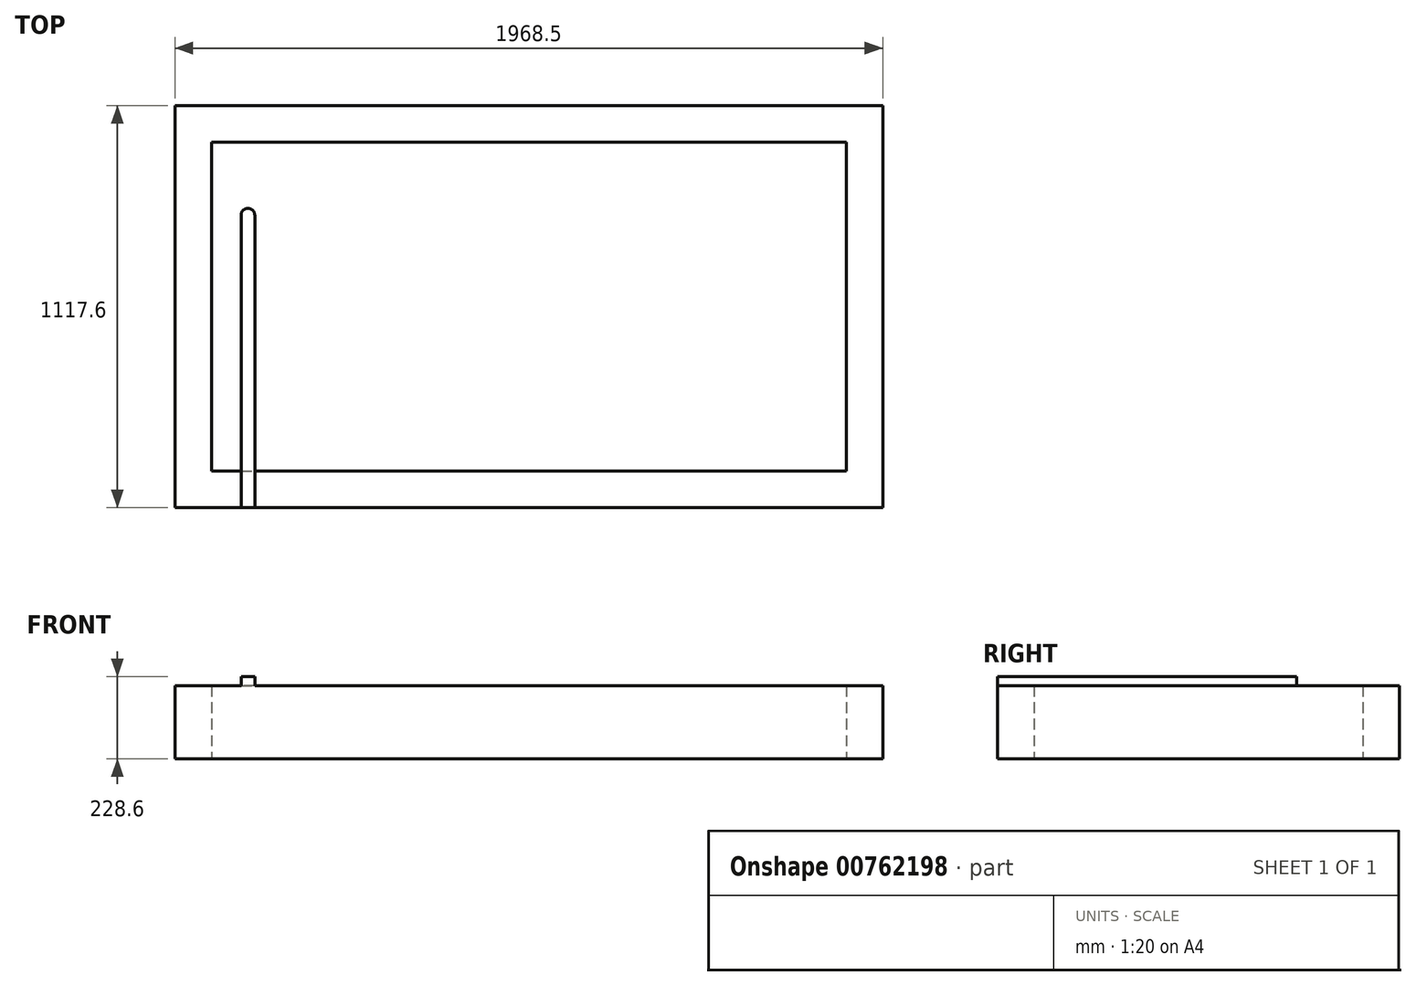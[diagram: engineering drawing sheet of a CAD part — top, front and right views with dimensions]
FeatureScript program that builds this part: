
annotation { "Feature Type Name" : "Feature", "Feature Type Description" : "" }
export const myFeature = defineFeature(function(context is Context, id is Id, definition is map)
    precondition{}
    {
        {
            var Q0;
            Q0=qCreatedBy(makeId("Top.planeOp"),FACE);
            var sketch = newSketch(context, id + "F0", { "sketchPlane" : qUnion([Q0])});
            skLineSegment(sketch, "E0.bottom", {"start": v(0, 0) * mm, "end": v(1968.5, 0) * mm});
            skLineSegment(sketch, "E0.top", {"start": v(0, -1117.6) * mm, "end": v(1968.5, -1117.6) * mm});
            skLineSegment(sketch, "E0.left", {"start": v(0, 0) * mm, "end": v(0, -1117.6) * mm});
            skLineSegment(sketch, "E0.right", {"start": v(1968.5, 0) * mm, "end": v(1968.5, -1117.6) * mm});
            skLineSegment(sketch, "E1.bottom", {"start": v(101.6, -101.6) * mm, "end": v(1866.9, -101.6) * mm});
            skLineSegment(sketch, "E1.top", {"start": v(101.6, -1016) * mm, "end": v(1866.9, -1016) * mm});
            skLineSegment(sketch, "E1.left", {"start": v(101.6, -101.6) * mm, "end": v(101.6, -1016) * mm});
            skLineSegment(sketch, "E1.right", {"start": v(1866.9, -101.6) * mm, "end": v(1866.9, -1016) * mm});
            skSolve(sketch);
        }
        {
            var Q0;
            Q0=makeQuery(id+"F0.imprint","IMPRINT",FACE,{"disambiguationData":[TD([[makeQuery(id+"F0.imprint","IMPRINT",EDGE,{"derivedFrom":sQuery(id+"F0.wireOp",EDGE,"E0.bottom")}),-1.0]])]});
            extrude(context, id + "F1", {"entities" : qUnion([Q0]), "depth" : 203.2 * mm, "offsetDistance" : 25.4 * mm});
        }
        {
            var Q0;
            Q0=makeQuery(id+"F1.opExtrude","CAP_FACE",FACE,{"disambiguationData":[OSD([sQuery(id+"F0.wireOp",EDGE,"E0.bottom"),sQuery(id+"F0.wireOp",EDGE,"E0.top"),sQuery(id+"F0.wireOp",EDGE,"E0.left"),sQuery(id+"F0.wireOp",EDGE,"E0.right"),sQuery(id+"F0.wireOp",EDGE,"E1.bottom"),sQuery(id+"F0.wireOp",EDGE,"E1.top"),sQuery(id+"F0.wireOp",EDGE,"E1.left"),sQuery(id+"F0.wireOp",EDGE,"E1.right")])],"isStart":false});
            var sketch = newSketch(context, id + "F2", { "sketchPlane" : qUnion([Q0])});
            skLineSegment(sketch, "E2", {"start": v(184.15, -304.8) * mm, "end": v(184.15, -1117.6) * mm});
            skLineSegment(sketch, "E3", {"start": v(222.25, -304.8) * mm, "end": v(222.25, -1117.6) * mm});
            skArc(sketch, "E4", {"start": v(222.25, -304.8) * mm, "mid": v(203.2, -285.75) * mm, "end": v(184.15, -304.8) * mm});
            skLineSegment(sketch, "E5", {"start": v(184.15, -1117.6) * mm, "end": v(222.25, -1117.6) * mm});
            skSolve(sketch);
        }
        {
            var Q0;
            Q0 = qSketchRegion(id + "F2", true);
            extrude(context, id + "F3", {"entities" : qUnion([Q0]), "operationType" : NewBodyOperationType.ADD, "depth" : 25.4 * mm, "offsetDistance" : 25.4 * mm});
        }
    });
